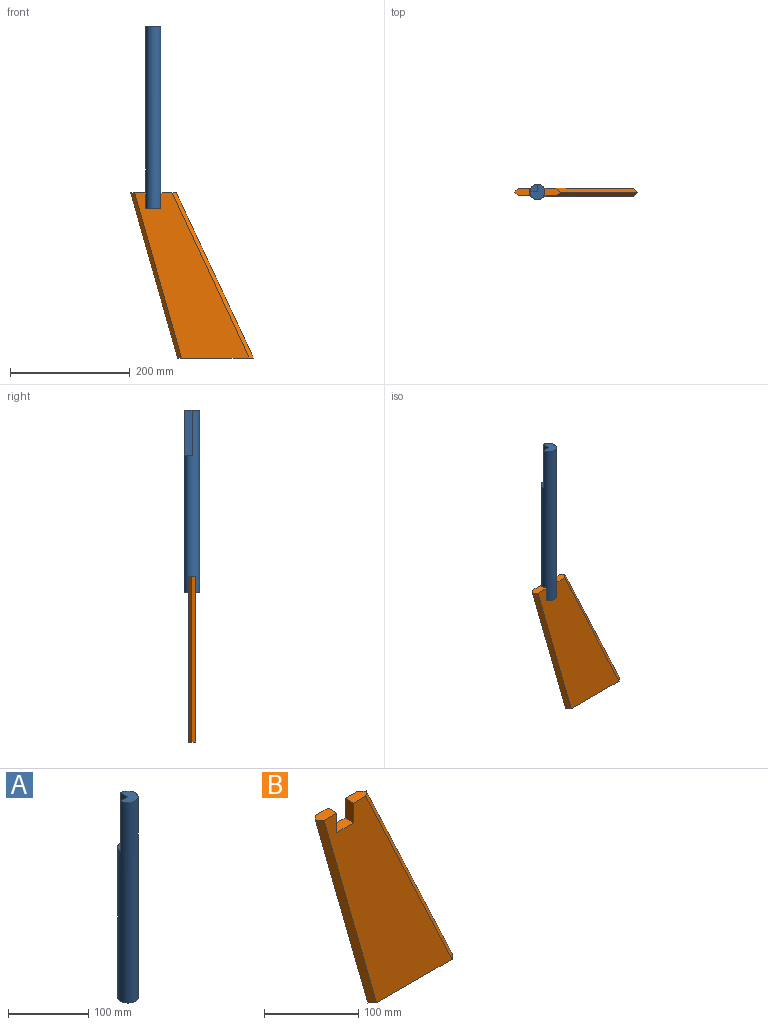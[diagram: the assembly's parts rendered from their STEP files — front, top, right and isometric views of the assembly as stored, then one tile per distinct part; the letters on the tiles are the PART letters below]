
ASSEMBLY  parts=2 mates=1
PART A: 6 faces, bbox 25.4x25.4x304.8 mm
  f0: plane 25.4x25.4mm, normal (0,0,1), area 380mm2, adj f1,f3,f4
  f1: cylinder r=12.7mm len=304.8mm, axis (0,0,-1), area 22801.8mm2, adj f0,f2,f3,f4,f5
  f2: plane 25.4x25.4mm, normal (0,0,-1), area 506.7mm2, adj f1
  f3: plane 76.2x12.7mm, normal (0,1,0), area 967.7mm2, adj f0,f1,f4,f5
  f4: plane 76.2x12.7mm, normal (-1,0,0), area 967.7mm2, adj f0,f1,f3,f5
  f5: plane 12.7x12.7mm, normal (0,0,1), area 126.7mm2, adj f1,f3,f4
PART B: 12 faces, bbox 205.4x12.7x276.1 mm
  f0: plane 25.4x12.7mm, normal (0,0,1), area 278.1mm2, adj f1,f4,f5,f8,f9
  f1: plane 276.07x191.78mm, normal (0,1,0), area 23645.4mm2, adj f0,f2,f3,f5,f6,f7,f8,f10
  f2: plane 127x12.7mm, normal (0,0,-1), area 1526.5mm2, adj f1,f4,f8,f9,f10,f11
  f3: plane 25.4x12.7mm, normal (0,0,1), area 280.7mm2, adj f1,f4,f7,f10,f11
  f4: plane 276.07x191.78mm, normal (0,-1,0), area 23645.4mm2, adj f0,f2,f3,f5,f6,f7,f9,f11
  f5: plane 25.4x12.7mm, normal (-1,0,0), area 322.6mm2, adj f0,f1,f4,f6
  f6: plane 25.4x12.7mm, normal (0,0,1), area 322.6mm2, adj f1,f4,f5,f7
  f7: plane 25.4x12.7mm, normal (1,0,0), area 322.6mm2, adj f1,f3,f4,f6
  f8: plane 276.07x136.2mm, normal (0.64,0.71,0.3), area 2737.2mm2, adj f0,f1,f2,f9
  f9: plane 276.07x136.2mm, normal (0.64,-0.71,0.3), area 2737.2mm2, adj f0,f2,f4,f8
  f10: plane 276.07x84.99mm, normal (-0.68,0.71,-0.19), area 2577.2mm2, adj f1,f2,f3,f11
  f11: plane 276.07x84.99mm, normal (-0.68,-0.71,-0.19), area 2577.2mm2, adj f2,f3,f4,f10
PLACE A t=(-19.83,178.83,-303.77)mm
PLACE B t=(7.38,195.11,-516.24)mm
MATE fastened B.f6 <-> A.f1  axis (0,0,1) through (-30.72,188.76,-303.77)mm
